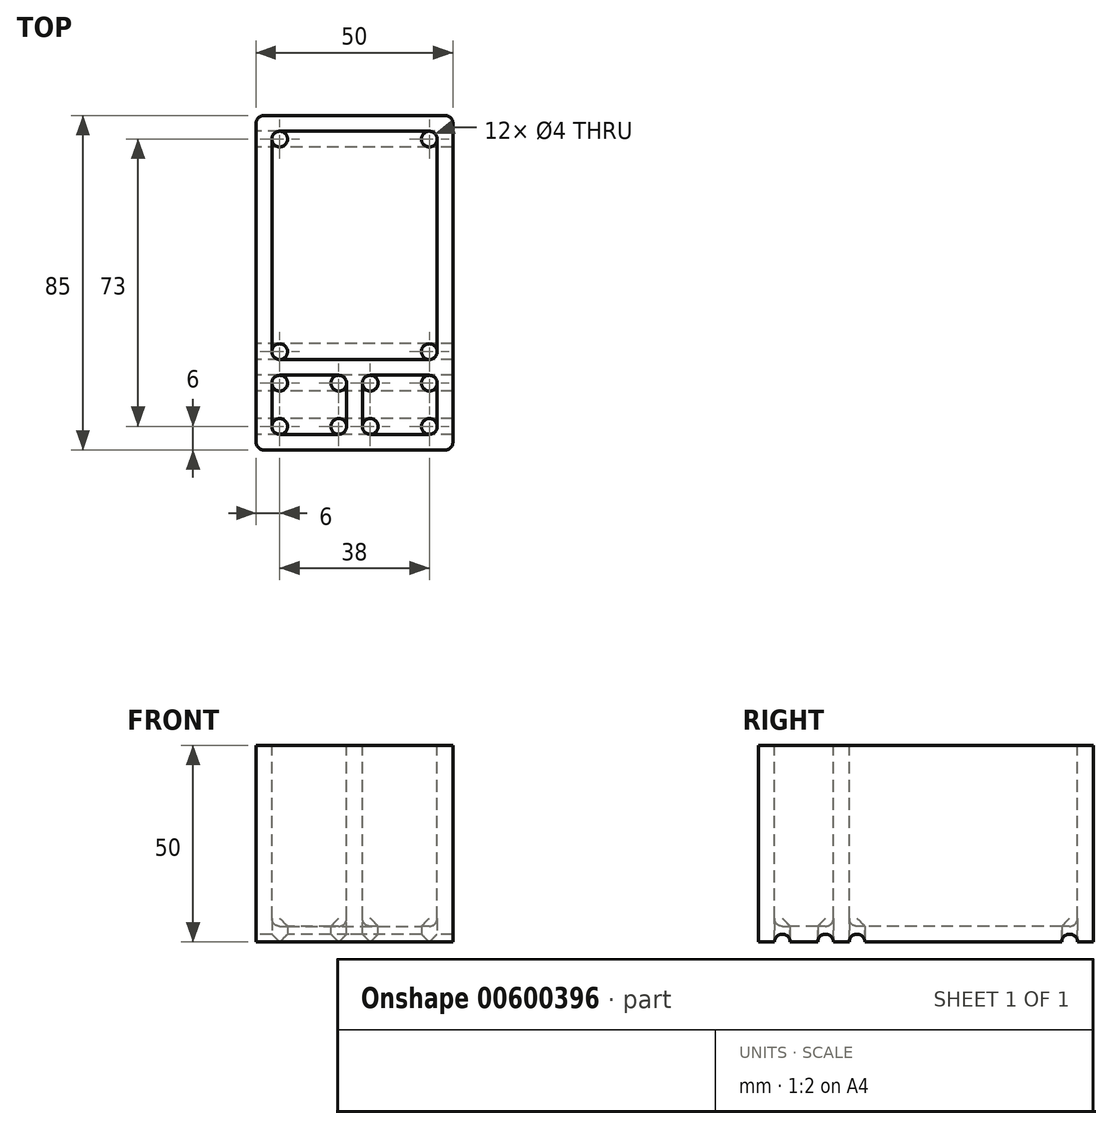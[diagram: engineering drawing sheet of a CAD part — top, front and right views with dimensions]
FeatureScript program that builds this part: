
annotation { "Feature Type Name" : "Feature", "Feature Type Description" : "" }
export const myFeature = defineFeature(function(context is Context, id is Id, definition is map)
    precondition{}
    {
        {
            var Q0;
            Q0=qCreatedBy(makeId("Top.planeOp"),FACE);
            var sketch = newSketch(context, id + "F0", { "sketchPlane" : qUnion([Q0])});
            skLineSegment(sketch, "E0.bottom", {"start": v(-25, 42.5) * mm, "end": v(25, 42.5) * mm});
            skLineSegment(sketch, "E0.top", {"start": v(-25, -42.5) * mm, "end": v(25, -42.5) * mm});
            skLineSegment(sketch, "E0.left", {"start": v(-25, 42.5) * mm, "end": v(-25, -42.5) * mm});
            skLineSegment(sketch, "E0.right", {"start": v(25, 42.5) * mm, "end": v(25, -42.5) * mm});
            skPoint(sketch, "E1", {"position": v(0, 0) * mm});
            skSolve(sketch);
        }
        {
            var Q0;
            Q0=makeQuery(id+"F0.imprint","IMPRINT",FACE,{"disambiguationData":[TD([[makeQuery(id+"F0.imprint","IMPRINT",EDGE,{"derivedFrom":sQuery(id+"F0.wireOp",EDGE,"E0.bottom")}),-1.0]])]});
            extrude(context, id + "F1", {"entities" : qUnion([Q0]), "depth" : 50 * mm, "offsetDistance" : 25 * mm});
        }
        {
            var Q0;
            Q0=makeQuery(id+"F1.opExtrude","CAP_FACE",FACE,{"disambiguationData":[OSD([sQuery(id+"F0.wireOp",EDGE,"E0.bottom"),sQuery(id+"F0.wireOp",EDGE,"E0.top"),sQuery(id+"F0.wireOp",EDGE,"E0.left"),sQuery(id+"F0.wireOp",EDGE,"E0.right")])],"isStart":false});
            var sketch = newSketch(context, id + "F2", { "sketchPlane" : qUnion([Q0])});
            skLineSegment(sketch, "E2.bottom", {"start": v(21, -19.5) * mm, "end": v(-21, -19.5) * mm});
            skLineSegment(sketch, "E2.top", {"start": v(21, 38.5) * mm, "end": v(-21, 38.5) * mm});
            skLineSegment(sketch, "E2.left", {"start": v(21, -19.5) * mm, "end": v(21, 38.5) * mm});
            skLineSegment(sketch, "E2.right", {"start": v(-21, -19.5) * mm, "end": v(-21, 38.5) * mm});
            skPoint(sketch, "E2.middle", {"position": v(0, 9.5) * mm});
            skLineSegment(sketch, "E3.bottom", {"start": v(21, -38.5) * mm, "end": v(2, -38.5) * mm});
            skLineSegment(sketch, "E3.top", {"start": v(21, -23.5) * mm, "end": v(2, -23.5) * mm});
            skLineSegment(sketch, "E3.left", {"start": v(21, -38.5) * mm, "end": v(21, -23.5) * mm});
            skLineSegment(sketch, "E3.right", {"start": v(2, -38.5) * mm, "end": v(2, -23.5) * mm});
            skPoint(sketch, "E3.middle", {"position": v(11.5, -31) * mm});
            skLineSegment(sketch, "E4", {"start": v(0, 42.5) * mm, "end": v(0, -42.5) * mm, "construction": true});
            skLineSegment(sketch, "E5.MirrorCS", {"start": v(-21, -23.5) * mm, "end": v(-2, -23.5) * mm});
            skLineSegment(sketch, "E6.MirrorCS", {"start": v(-2, -38.5) * mm, "end": v(-2, -23.5) * mm});
            skLineSegment(sketch, "E7.MirrorCS", {"start": v(-21, -38.5) * mm, "end": v(-2, -38.5) * mm});
            skLineSegment(sketch, "E8.MirrorCS", {"start": v(-21, -38.5) * mm, "end": v(-21, -23.5) * mm});
            skSolve(sketch);
        }
        {
            var Q0;
            Q0=makeQuery(id+"F2.imprint","IMPRINT",FACE,{"disambiguationData":[TD([[makeQuery(id+"F2.imprint","IMPRINT",EDGE,{"derivedFrom":sQuery(id+"F2.wireOp",EDGE,"E2.bottom")}),-1.0]])]});
            var Q1;
            Q1=makeQuery(id+"F2.imprint","IMPRINT",FACE,{"disambiguationData":[TD([[makeQuery(id+"F2.imprint","IMPRINT",EDGE,{"derivedFrom":sQuery(id+"F2.wireOp",EDGE,"E5.MirrorCS")}),-1.0]])]});
            var Q2;
            Q2=makeQuery(id+"F2.imprint","IMPRINT",FACE,{"disambiguationData":[TD([[makeQuery(id+"F2.imprint","IMPRINT",EDGE,{"derivedFrom":sQuery(id+"F2.wireOp",EDGE,"E3.bottom")}),-1.0]])]});
            var Q3;
            Q3=sQuery(id+"F2.wireOp",EDGE,"czfywLNU-dvi0-LOzS-A4PM-ZlCnxevdbvJO.top");
            var Q4;
            Q4=sQuery(id+"F2.wireOp",EDGE,"czfywLNU-dvi0-LOzS-A4PM-ZlCnxevdbvJO.left");
            var Q5;
            Q5=sQuery(id+"F2.wireOp",EDGE,"czfywLNU-dvi0-LOzS-A4PM-ZlCnxevdbvJO.bottom");
            var Q6;
            Q6=sQuery(id+"F2.wireOp",EDGE,"czfywLNU-dvi0-LOzS-A4PM-ZlCnxevdbvJO.right");
            var Q7;
            Q7=sQuery(id+"F2.wireOp",EDGE,"E3.right");
            var Q8;
            Q8=sQuery(id+"F2.wireOp",EDGE,"E3.bottom");
            var Q9;
            Q9=sQuery(id+"F2.wireOp",EDGE,"E3.left");
            var Q10;
            Q10=sQuery(id+"F2.wireOp",EDGE,"E3.top");
            var Q11;
            Q11=sQuery(id+"F2.wireOp",EDGE,"E2.top");
            var Q12;
            Q12=sQuery(id+"F2.wireOp",EDGE,"E2.right");
            var Q13;
            Q13=sQuery(id+"F2.wireOp",EDGE,"E2.bottom");
            var Q14;
            Q14=sQuery(id+"F2.wireOp",EDGE,"E2.left");
            var Q15;
            Q15=makeQuery(id+"F1.opExtrude","CAP_FACE",FACE,{"disambiguationData":[OSD([sQuery(id+"F0.wireOp",EDGE,"E0.bottom"),sQuery(id+"F0.wireOp",EDGE,"E0.top"),sQuery(id+"F0.wireOp",EDGE,"E0.left"),sQuery(id+"F0.wireOp",EDGE,"E0.right")])],"isStart":true});
            extrude(context, id + "F3", {"entities" : qUnion([Q0, Q1, Q2]), "operationType" : NewBodyOperationType.REMOVE, "surfaceEntities" : qUnion([Q3, Q4, Q5, Q6, Q7, Q8, Q9, Q10, Q11, Q12, Q13, Q14]), "endBound" : BoundingType.UP_TO_SURFACE, "oppositeDirection" : true, "depth" : 70 * mm, "endBoundEntityFace" : qUnion([Q15]), "hasOffset" : true, "offsetDistance" : 4 * mm});
        }
        {
            var Q0;
            Q0=makeQuery(id+"F3.boolean.opBoolean","COPY",EDGE,{"derivedFrom":makeQuery(id+"F3.opExtrude","CAP_EDGE",EDGE,{"disambiguationData":[OSD([sQuery(id+"F2.wireOp",EDGE,"E2.right")])],"isStart":false})});
            var Q1;
            Q1=makeQuery(id+"F3.boolean.opBoolean","COPY",EDGE,{"derivedFrom":makeQuery(id+"F3.opExtrude","CAP_EDGE",EDGE,{"disambiguationData":[OSD([sQuery(id+"F2.wireOp",EDGE,"E2.top")])],"isStart":false})});
            var Q2;
            Q2=makeQuery(id+"F3.boolean.opBoolean","COPY",EDGE,{"derivedFrom":makeQuery(id+"F3.opExtrude","CAP_EDGE",EDGE,{"disambiguationData":[OSD([sQuery(id+"F2.wireOp",EDGE,"E2.left")])],"isStart":false})});
            var Q3;
            Q3=makeQuery(id+"F3.boolean.opBoolean","COPY",EDGE,{"derivedFrom":makeQuery(id+"F3.opExtrude","CAP_EDGE",EDGE,{"disambiguationData":[OSD([sQuery(id+"F2.wireOp",EDGE,"E2.bottom")])],"isStart":false})});
            var Q4;
            Q4=makeQuery(id+"F3.boolean.opBoolean","COPY",EDGE,{"derivedFrom":makeQuery(id+"F3.opExtrude","CAP_EDGE",EDGE,{"disambiguationData":[OSD([sQuery(id+"F2.wireOp",EDGE,"E3.left")])],"isStart":false})});
            var Q5;
            Q5=makeQuery(id+"F3.boolean.opBoolean","COPY",EDGE,{"derivedFrom":makeQuery(id+"F3.opExtrude","CAP_EDGE",EDGE,{"disambiguationData":[OSD([sQuery(id+"F2.wireOp",EDGE,"E3.bottom")])],"isStart":false})});
            var Q6;
            Q6=makeQuery(id+"F3.boolean.opBoolean","COPY",EDGE,{"derivedFrom":makeQuery(id+"F3.opExtrude","TWEAK_EDGE",EDGE,{"derivedFrom":[makeQuery(id+"F1.opExtrude","CAP_FACE",FACE,{"disambiguationData":[OSD([sQuery(id+"F0.wireOp",EDGE,"E0.bottom"),sQuery(id+"F0.wireOp",EDGE,"E0.top"),sQuery(id+"F0.wireOp",EDGE,"E0.left"),sQuery(id+"F0.wireOp",EDGE,"E0.right")])],"isStart":true}),makeQuery(id+"F2.imprint","IMPRINT",EDGE,{"derivedFrom":sQuery(id+"F2.wireOp",EDGE,"czfywLNU-dvi0-LOzS-A4PM-ZlCnxevdbvJO.bottom")})]})});
            var Q7;
            Q7=makeQuery(id+"F3.boolean.opBoolean","COPY",EDGE,{"derivedFrom":makeQuery(id+"F3.opExtrude","TWEAK_EDGE",EDGE,{"derivedFrom":[makeQuery(id+"F1.opExtrude","CAP_FACE",FACE,{"disambiguationData":[OSD([sQuery(id+"F0.wireOp",EDGE,"E0.bottom"),sQuery(id+"F0.wireOp",EDGE,"E0.top"),sQuery(id+"F0.wireOp",EDGE,"E0.left"),sQuery(id+"F0.wireOp",EDGE,"E0.right")])],"isStart":true}),makeQuery(id+"F2.imprint","IMPRINT",EDGE,{"derivedFrom":sQuery(id+"F2.wireOp",EDGE,"czfywLNU-dvi0-LOzS-A4PM-ZlCnxevdbvJO.right")})]})});
            var Q8;
            Q8=makeQuery(id+"F3.boolean.opBoolean","COPY",EDGE,{"derivedFrom":makeQuery(id+"F3.opExtrude","TWEAK_EDGE",EDGE,{"derivedFrom":[makeQuery(id+"F1.opExtrude","CAP_FACE",FACE,{"disambiguationData":[OSD([sQuery(id+"F0.wireOp",EDGE,"E0.bottom"),sQuery(id+"F0.wireOp",EDGE,"E0.top"),sQuery(id+"F0.wireOp",EDGE,"E0.left"),sQuery(id+"F0.wireOp",EDGE,"E0.right")])],"isStart":true}),makeQuery(id+"F2.imprint","IMPRINT",EDGE,{"derivedFrom":sQuery(id+"F2.wireOp",EDGE,"czfywLNU-dvi0-LOzS-A4PM-ZlCnxevdbvJO.top")})]})});
            var Q9;
            Q9=makeQuery(id+"F3.boolean.opBoolean","COPY",EDGE,{"derivedFrom":makeQuery(id+"F3.opExtrude","TWEAK_EDGE",EDGE,{"derivedFrom":[makeQuery(id+"F1.opExtrude","CAP_FACE",FACE,{"disambiguationData":[OSD([sQuery(id+"F0.wireOp",EDGE,"E0.bottom"),sQuery(id+"F0.wireOp",EDGE,"E0.top"),sQuery(id+"F0.wireOp",EDGE,"E0.left"),sQuery(id+"F0.wireOp",EDGE,"E0.right")])],"isStart":true}),makeQuery(id+"F2.imprint","IMPRINT",EDGE,{"derivedFrom":sQuery(id+"F2.wireOp",EDGE,"czfywLNU-dvi0-LOzS-A4PM-ZlCnxevdbvJO.left")})]})});
            var Q10;
            Q10=makeQuery(id+"F3.boolean.opBoolean","COPY",EDGE,{"derivedFrom":makeQuery(id+"F3.opExtrude","CAP_EDGE",EDGE,{"disambiguationData":[OSD([sQuery(id+"F2.wireOp",EDGE,"E3.right")])],"isStart":false})});
            var Q11;
            Q11=makeQuery(id+"F3.boolean.opBoolean","COPY",EDGE,{"derivedFrom":makeQuery(id+"F3.opExtrude","CAP_EDGE",EDGE,{"disambiguationData":[OSD([sQuery(id+"F2.wireOp",EDGE,"E3.top")])],"isStart":false})});
            var Q12;
            Q12=makeQuery(id+"F1.opExtrude","SWEPT_EDGE",EDGE,{"disambiguationData":[OSD([sQuery(id+"F0.wireOp",EDGE,"E0.bottom"),sQuery(id+"F0.wireOp",EDGE,"E0.left")])]});
            var Q13;
            Q13=makeQuery(id+"F1.opExtrude","SWEPT_EDGE",EDGE,{"disambiguationData":[OSD([sQuery(id+"F0.wireOp",EDGE,"E0.top"),sQuery(id+"F0.wireOp",EDGE,"E0.left")])]});
            var Q14;
            Q14=makeQuery(id+"F1.opExtrude","SWEPT_EDGE",EDGE,{"disambiguationData":[OSD([sQuery(id+"F0.wireOp",EDGE,"E0.top"),sQuery(id+"F0.wireOp",EDGE,"E0.right")])]});
            var Q15;
            Q15=makeQuery(id+"F1.opExtrude","SWEPT_EDGE",EDGE,{"disambiguationData":[OSD([sQuery(id+"F0.wireOp",EDGE,"E0.bottom"),sQuery(id+"F0.wireOp",EDGE,"E0.right")])]});
            var Q16;
            Q16=makeQuery(id+"F3.boolean.opBoolean","COPY",EDGE,{"derivedFrom":makeQuery(id+"F3.opExtrude","SWEPT_EDGE",EDGE,{"disambiguationData":[OSD([sQuery(id+"F2.wireOp",EDGE,"E2.top"),sQuery(id+"F2.wireOp",EDGE,"E2.right")])]})});
            var Q17;
            Q17=makeQuery(id+"F3.boolean.opBoolean","COPY",EDGE,{"derivedFrom":makeQuery(id+"F3.opExtrude","SWEPT_EDGE",EDGE,{"disambiguationData":[OSD([sQuery(id+"F2.wireOp",EDGE,"E2.top"),sQuery(id+"F2.wireOp",EDGE,"E2.left")])]})});
            var Q18;
            Q18=makeQuery(id+"F3.boolean.opBoolean","COPY",EDGE,{"derivedFrom":makeQuery(id+"F3.opExtrude","SWEPT_EDGE",EDGE,{"disambiguationData":[OSD([sQuery(id+"F2.wireOp",EDGE,"E2.bottom"),sQuery(id+"F2.wireOp",EDGE,"E2.left")])]})});
            var Q19;
            Q19=makeQuery(id+"F3.boolean.opBoolean","COPY",EDGE,{"derivedFrom":makeQuery(id+"F3.opExtrude","SWEPT_EDGE",EDGE,{"disambiguationData":[OSD([sQuery(id+"F2.wireOp",EDGE,"E2.bottom"),sQuery(id+"F2.wireOp",EDGE,"E2.right")])]})});
            var Q20;
            Q20=makeQuery(id+"F3.boolean.opBoolean","COPY",EDGE,{"derivedFrom":makeQuery(id+"F3.opExtrude","SWEPT_EDGE",EDGE,{"disambiguationData":[OSD([sQuery(id+"F2.wireOp",EDGE,"czfywLNU-dvi0-LOzS-A4PM-ZlCnxevdbvJO.bottom"),sQuery(id+"F2.wireOp",EDGE,"czfywLNU-dvi0-LOzS-A4PM-ZlCnxevdbvJO.right")])]})});
            var Q21;
            Q21=makeQuery(id+"F3.boolean.opBoolean","COPY",EDGE,{"derivedFrom":makeQuery(id+"F3.opExtrude","SWEPT_EDGE",EDGE,{"disambiguationData":[OSD([sQuery(id+"F2.wireOp",EDGE,"czfywLNU-dvi0-LOzS-A4PM-ZlCnxevdbvJO.top"),sQuery(id+"F2.wireOp",EDGE,"czfywLNU-dvi0-LOzS-A4PM-ZlCnxevdbvJO.right")])]})});
            var Q22;
            Q22=makeQuery(id+"F3.boolean.opBoolean","COPY",EDGE,{"derivedFrom":makeQuery(id+"F3.opExtrude","SWEPT_EDGE",EDGE,{"disambiguationData":[OSD([sQuery(id+"F2.wireOp",EDGE,"czfywLNU-dvi0-LOzS-A4PM-ZlCnxevdbvJO.top"),sQuery(id+"F2.wireOp",EDGE,"czfywLNU-dvi0-LOzS-A4PM-ZlCnxevdbvJO.left")])]})});
            var Q23;
            Q23=makeQuery(id+"F3.boolean.opBoolean","COPY",EDGE,{"derivedFrom":makeQuery(id+"F3.opExtrude","SWEPT_EDGE",EDGE,{"disambiguationData":[OSD([sQuery(id+"F2.wireOp",EDGE,"E3.top"),sQuery(id+"F2.wireOp",EDGE,"E3.right")])]})});
            var Q24;
            Q24=makeQuery(id+"F3.boolean.opBoolean","COPY",EDGE,{"derivedFrom":makeQuery(id+"F3.opExtrude","SWEPT_EDGE",EDGE,{"disambiguationData":[OSD([sQuery(id+"F2.wireOp",EDGE,"czfywLNU-dvi0-LOzS-A4PM-ZlCnxevdbvJO.bottom"),sQuery(id+"F2.wireOp",EDGE,"czfywLNU-dvi0-LOzS-A4PM-ZlCnxevdbvJO.left")])]})});
            var Q25;
            Q25=makeQuery(id+"F3.boolean.opBoolean","COPY",EDGE,{"derivedFrom":makeQuery(id+"F3.opExtrude","SWEPT_EDGE",EDGE,{"disambiguationData":[OSD([sQuery(id+"F2.wireOp",EDGE,"E3.bottom"),sQuery(id+"F2.wireOp",EDGE,"E3.left")])]})});
            var Q26;
            Q26=makeQuery(id+"F3.boolean.opBoolean","COPY",EDGE,{"derivedFrom":makeQuery(id+"F3.opExtrude","SWEPT_EDGE",EDGE,{"disambiguationData":[OSD([sQuery(id+"F2.wireOp",EDGE,"E3.top"),sQuery(id+"F2.wireOp",EDGE,"E3.left")])]})});
            var Q27;
            Q27=makeQuery(id+"F3.boolean.opBoolean","COPY",EDGE,{"derivedFrom":makeQuery(id+"F3.opExtrude","SWEPT_EDGE",EDGE,{"disambiguationData":[OSD([sQuery(id+"F2.wireOp",EDGE,"E3.bottom"),sQuery(id+"F2.wireOp",EDGE,"E3.right")])]})});
            var Q28;
            Q28=makeQuery(id+"F3.boolean.opBoolean","COPY",EDGE,{"derivedFrom":makeQuery(id+"F3.opExtrude","CAP_EDGE",EDGE,{"disambiguationData":[OSD([sQuery(id+"F2.wireOp",EDGE,"E8.MirrorCS")])],"isStart":false})});
            var Q29;
            Q29=makeQuery(id+"F3.boolean.opBoolean","COPY",EDGE,{"derivedFrom":makeQuery(id+"F3.opExtrude","SWEPT_EDGE",EDGE,{"disambiguationData":[OSD([sQuery(id+"F2.wireOp",EDGE,"E5.MirrorCS"),sQuery(id+"F2.wireOp",EDGE,"E8.MirrorCS")])]})});
            var Q30;
            Q30=makeQuery(id+"F3.boolean.opBoolean","COPY",EDGE,{"derivedFrom":makeQuery(id+"F3.opExtrude","CAP_EDGE",EDGE,{"disambiguationData":[OSD([sQuery(id+"F2.wireOp",EDGE,"E5.MirrorCS")])],"isStart":false})});
            var Q31;
            Q31=makeQuery(id+"F3.boolean.opBoolean","COPY",EDGE,{"derivedFrom":makeQuery(id+"F3.opExtrude","SWEPT_EDGE",EDGE,{"disambiguationData":[OSD([sQuery(id+"F2.wireOp",EDGE,"E5.MirrorCS"),sQuery(id+"F2.wireOp",EDGE,"E6.MirrorCS")])]})});
            var Q32;
            Q32=makeQuery(id+"F3.boolean.opBoolean","COPY",EDGE,{"derivedFrom":makeQuery(id+"F3.opExtrude","CAP_EDGE",EDGE,{"disambiguationData":[OSD([sQuery(id+"F2.wireOp",EDGE,"E6.MirrorCS")])],"isStart":false})});
            var Q33;
            Q33=makeQuery(id+"F3.boolean.opBoolean","COPY",EDGE,{"derivedFrom":makeQuery(id+"F3.opExtrude","CAP_EDGE",EDGE,{"disambiguationData":[OSD([sQuery(id+"F2.wireOp",EDGE,"E7.MirrorCS")])],"isStart":false})});
            var Q34;
            Q34=makeQuery(id+"F3.boolean.opBoolean","COPY",EDGE,{"derivedFrom":makeQuery(id+"F3.opExtrude","SWEPT_EDGE",EDGE,{"disambiguationData":[OSD([sQuery(id+"F2.wireOp",EDGE,"E6.MirrorCS"),sQuery(id+"F2.wireOp",EDGE,"E7.MirrorCS")])]})});
            var Q35;
            Q35=makeQuery(id+"F3.boolean.opBoolean","COPY",EDGE,{"derivedFrom":makeQuery(id+"F3.opExtrude","SWEPT_EDGE",EDGE,{"disambiguationData":[OSD([sQuery(id+"F2.wireOp",EDGE,"E7.MirrorCS"),sQuery(id+"F2.wireOp",EDGE,"E8.MirrorCS")])]})});
            fillet(context, id + "F4", {"entities" : qUnion([Q0, Q1, Q2, Q3, Q4, Q5, Q6, Q7, Q8, Q9, Q10, Q11, Q12, Q13, Q14, Q15, Q16, Q17, Q18, Q19, Q20, Q21, Q22, Q23, Q24, Q25, Q26, Q27, Q28, Q29, Q30, Q31, Q32, Q33, Q34, Q35]), "radius" : 2 * mm, "tangentPropagation" : true, "allowEdgeOverflow" : false});
        }
        {
            var Q0;
            Q0=makeQuery(id+"F0.imprint","IMPRINT",FACE,{"disambiguationData":[TD([[makeQuery(id+"F0.imprint","IMPRINT",EDGE,{"derivedFrom":sQuery(id+"F0.wireOp",EDGE,"E0.bottom")}),-1.0]])]});
            var sketch = newSketch(context, id + "F5", { "sketchPlane" : qUnion([Q0])});
            skCircle(sketch, "E9", {"center": v(19, 36.5) * mm, "radius": 2 * mm});
            skCircle(sketch, "E10", {"center": v(19, -25.5) * mm, "radius": 2 * mm});
            skCircle(sketch, "E11", {"center": v(19, -36.5) * mm, "radius": 2 * mm});
            skCircle(sketch, "E12", {"center": v(4, -25.5) * mm, "radius": 2 * mm});
            skCircle(sketch, "E13", {"center": v(4, -36.5) * mm, "radius": 2 * mm});
            skCircle(sketch, "E14", {"center": v(19, -17.5) * mm, "radius": 2 * mm});
            skCircle(sketch, "E15.MirrorC", {"center": v(-19, 36.5) * mm, "radius": 2 * mm});
            skCircle(sketch, "E16.MirrorC", {"center": v(-19, -17.5) * mm, "radius": 2 * mm});
            skCircle(sketch, "E17.MirrorC", {"center": v(-19, -25.5) * mm, "radius": 2 * mm});
            skCircle(sketch, "E18.MirrorC", {"center": v(-4, -25.5) * mm, "radius": 2 * mm});
            skCircle(sketch, "E19.MirrorC", {"center": v(-4, -36.5) * mm, "radius": 2 * mm});
            skCircle(sketch, "E20.MirrorC", {"center": v(-19, -36.5) * mm, "radius": 2 * mm});
            skLineSegment(sketch, "E21", {"start": v(-19, 34.5) * mm, "end": v(-25, 34.5) * mm, "construction": true});
            skLineSegment(sketch, "E22", {"start": v(-19, -19.5) * mm, "end": v(-25, -19.5) * mm, "construction": true});
            skLineSegment(sketch, "E23", {"start": v(-19, -27.5) * mm, "end": v(-25, -27.5) * mm, "construction": true});
            skLineSegment(sketch, "E24", {"start": v(-19, -38.5) * mm, "end": v(-25, -38.5) * mm, "construction": true});
            skSolve(sketch);
        }
        {
            var Q0;
            Q0 = qSketchRegion(id + "F5", true);
            extrude(context, id + "F6", {"entities" : qUnion([Q0]), "operationType" : NewBodyOperationType.REMOVE, "endBound" : BoundingType.THROUGH_ALL, "depth" : 25 * mm, "offsetDistance" : 25 * mm});
        }
        {
            var Q0;
            Q0=makeQuery(id+"F1.opExtrude","SWEPT_FACE",FACE,{"disambiguationData":[OSD([sQuery(id+"F0.wireOp",EDGE,"E0.left")])]});
            var sketch = newSketch(context, id + "F7", { "sketchPlane" : qUnion([Q0])});
            skCircle(sketch, "E25", {"center": v(-36.5, 0) * mm, "radius": 2 * mm});
            skCircle(sketch, "E26", {"center": v(17.5, 0) * mm, "radius": 2 * mm});
            skCircle(sketch, "E27", {"center": v(25.5, 0) * mm, "radius": 2 * mm});
            skCircle(sketch, "E28", {"center": v(36.5, 0) * mm, "radius": 2 * mm});
            skSolve(sketch);
        }
        {
            var Q0;
            Q0 = qSketchRegion(id + "F7", true);
            extrude(context, id + "F8", {"entities" : qUnion([Q0]), "operationType" : NewBodyOperationType.REMOVE, "endBound" : BoundingType.THROUGH_ALL, "oppositeDirection" : true, "depth" : 25 * mm, "offsetDistance" : 25 * mm});
        }
    });
